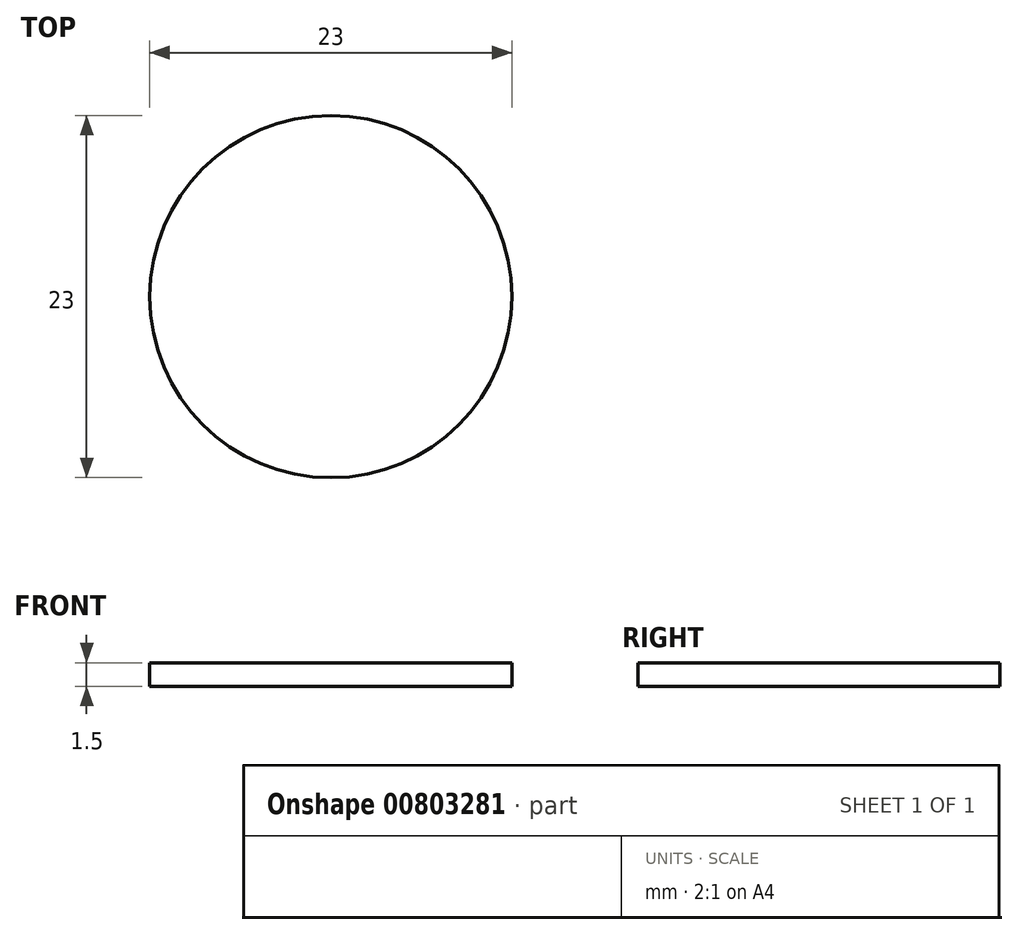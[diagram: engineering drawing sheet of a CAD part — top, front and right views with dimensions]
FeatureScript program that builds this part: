
annotation { "Feature Type Name" : "Feature", "Feature Type Description" : "" }
export const myFeature = defineFeature(function(context is Context, id is Id, definition is map)
    precondition{}
    {
        {
            var Q0;
            Q0=qCreatedBy(makeId("Top.planeOp"),FACE);
            var sketch = newSketch(context, id + "F0", { "sketchPlane" : qUnion([Q0])});
            skCircle(sketch, "E0", {"center": v(0, 0) * mm, "radius": 11.5 * mm});
            skSolve(sketch);
        }
        {
            var Q0;
            Q0=makeQuery(id+"F0.imprint","IMPRINT",FACE,{"disambiguationData":[TD([[makeQuery(id+"F0.imprint","IMPRINT",EDGE,{"derivedFrom":sQuery(id+"F0.wireOp",EDGE,"E0")}),1.0]])]});
            extrude(context, id + "F1", {"entities" : qUnion([Q0]), "depth" : 1.5 * mm, "offsetDistance" : 25 * mm});
        }
    });
